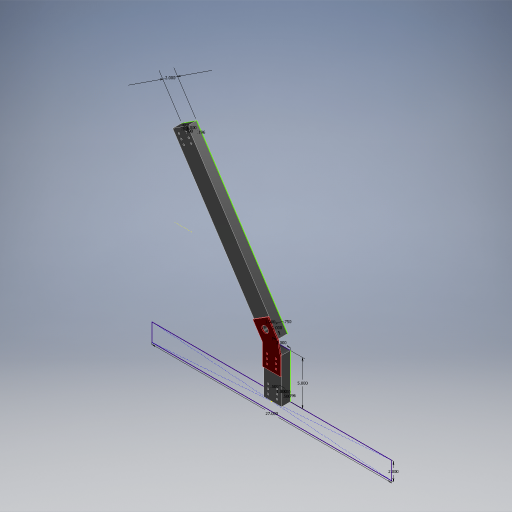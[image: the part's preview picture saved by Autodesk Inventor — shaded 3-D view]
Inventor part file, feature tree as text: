
AUTODESK INVENTOR PART (.ipt)
format: ipt  version: 2024.2 (Build 282272000, 272)  size: 396,288 bytes
history: native  units: in
note: dims shown in document units (in); Inventor stores cm internally (conversion verified against a paired STEP export)
features: extrude x3, sketch x2, projected_geometry x2
ambient origin geometry x8: Origin, YZ Plane, XZ Plane, XY Plane, X Axis, Y Axis, Z Axis, Center Point
bodies: Solid5 (feature_tree), Solid6 (feature_tree)
feature tree (7):
  sketch  "Sketch1"  dims[d0=27.0in d1=2.0in]
  extrude  "Extrusion8"  Depth=2.0in
  extrude  "Extrusion9"  Depth=0.125in
  extrude  "Extrusion10"  Depth=0.125in
  sketch  "Sketch7"  dims[d5=5.0in d21=0.196in d22=0.5in d23=0.5in d24=0.7874in d26=1.0in d27=1.1811in d29=0.5in d60=2.0in d61=2.0in d62=0.196in d63=0.5in d64=0.5in d65=0.7874in d67=1.0in d68=1.1811in d70=0.5in d73=0.75in d74=1.0in d75=1.0in d76=1.0in d77=0.0in d78=1.0in d79=0.0in d80=2.0in d81=2.0in d82=0.125in d83=0.0in d46=0.5in d47=0.0344in d48=0.5in d49=0.0344in d50=0.5in d51=0.0344in d52=0.5in d53=0.0344in d54=0.5in d55=0.0344in]
  projected_geometry  "Projected Loop5"
  projected_geometry  "Projected Loop6"
